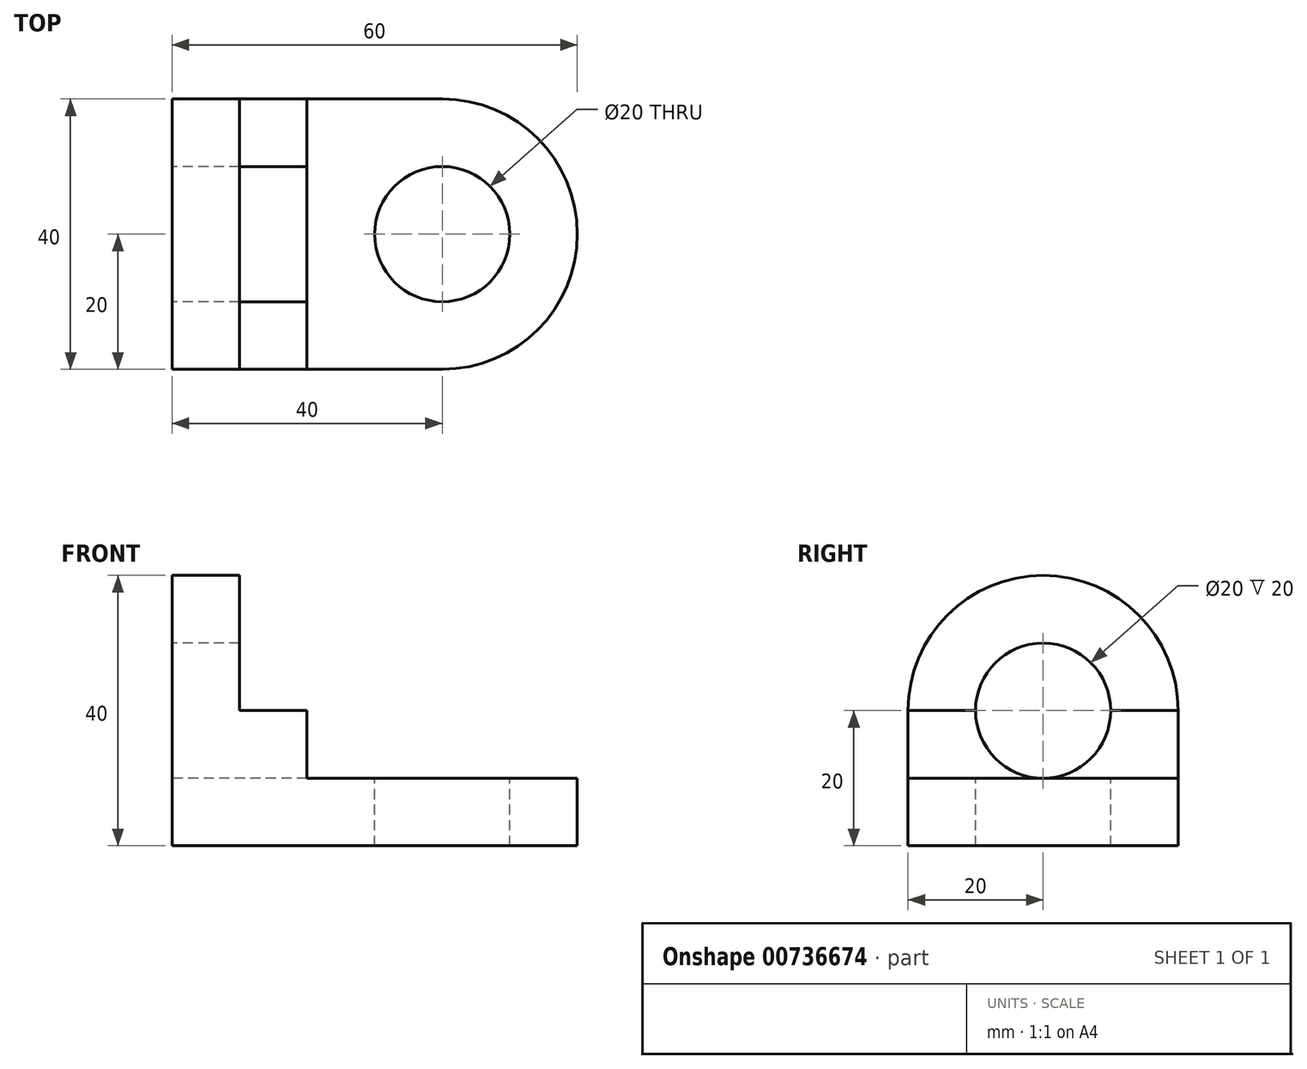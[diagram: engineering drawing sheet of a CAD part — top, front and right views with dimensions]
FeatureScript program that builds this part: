
annotation { "Feature Type Name" : "Feature", "Feature Type Description" : "" }
export const myFeature = defineFeature(function(context is Context, id is Id, definition is map)
    precondition{}
    {
        {
            var Q0;
            Q0=qCreatedBy(makeId("Right.planeOp"),FACE);
            var sketch = newSketch(context, id + "F0", { "sketchPlane" : qUnion([Q0])});
            skLineSegment(sketch, "E0", {"start": v(0, 0) * mm, "end": v(40, 0) * mm});
            skLineSegment(sketch, "E1", {"start": v(40, 0) * mm, "end": v(40, 40) * mm});
            skLineSegment(sketch, "E2", {"start": v(40, 40) * mm, "end": v(0, 40) * mm});
            skLineSegment(sketch, "E3", {"start": v(0, 40) * mm, "end": v(0, 0) * mm});
            skSolve(sketch);
        }
        {
            var Q0;
            Q0 = qSketchRegion(id + "F0", true);
            extrude(context, id + "F1", {"entities" : qUnion([Q0]), "depth" : 60 * mm, "offsetDistance" : 25 * mm});
        }
        {
            var Q0;
            Q0=makeQuery(id+"F1.opExtrude","SWEPT_FACE",FACE,{"disambiguationData":[OSD([sQuery(id+"F0.wireOp",EDGE,"E2")])]});
            var sketch = newSketch(context, id + "F2", { "sketchPlane" : qUnion([Q0])});
            skLineSegment(sketch, "E4", {"start": v(0, 40) * mm, "end": v(40, 40) * mm});
            skArc(sketch, "E5", {"start": v(40, 0) * mm, "mid": v(60, 20) * mm, "end": v(40, 40) * mm});
            skCircle(sketch, "E6", {"center": v(40, 20) * mm, "radius": 10 * mm});
            skSolve(sketch);
        }
        {
            var Q0;
            Q0=makeQuery(id+"F2.imprint","IMPRINT",FACE,{"disambiguationData":[TD([[makeQuery(id+"F2.imprint","IMPRINT",EDGE,{"derivedFrom":sQuery(id+"F2.wireOp",EDGE,"E6")}),1.0]])]});
            var Q1;
            {var subQ0=sQuery(id+"F2.wireOp",EDGE,"E5");var subQ1=sQuery(id+"F0.wireOp",EDGE,"E2");var subQ4=makeQuery(id+"F1.opExtrude","CAP_EDGE",EDGE,{"disambiguationData":[OSD([subQ1])],"isStart":false});var subQ5=makeQuery(id+"F2.imprint","INTERSECT",VERTEX,{"derivedFrom":[subQ4,subQ0]});Q1=makeQuery(id+"F2.imprint","IMPRINT",FACE,{"disambiguationData":[TD([[makeQuery(id+"F2.imprint","IMPRINT",EDGE,{"disambiguationData":[TD([[subQ5,1.0]])],"derivedFrom":subQ4}),-1.0]])]});}
            var Q2;
            {var subQ0=sQuery(id+"F2.wireOp",EDGE,"E5");var subQ1=sQuery(id+"F0.wireOp",EDGE,"E2");var subQ4=makeQuery(id+"F1.opExtrude","CAP_EDGE",EDGE,{"disambiguationData":[OSD([subQ1])],"isStart":false});var subQ5=makeQuery(id+"F2.imprint","INTERSECT",VERTEX,{"derivedFrom":[subQ4,subQ0]});Q2=makeQuery(id+"F2.imprint","IMPRINT",FACE,{"disambiguationData":[TD([[makeQuery(id+"F2.imprint","IMPRINT",EDGE,{"disambiguationData":[TD([[subQ5,1.0]])],"derivedFrom":subQ0}),-1.0]])]});}
            extrude(context, id + "F3", {"entities" : qUnion([Q0, Q1, Q2]), "operationType" : NewBodyOperationType.REMOVE, "oppositeDirection" : true, "depth" : 40 * mm, "offsetDistance" : 25 * mm});
        }
        {
            var Q0;
            Q0=makeQuery(id+"F1.opExtrude","CAP_FACE",FACE,{"disambiguationData":[OSD([sQuery(id+"F0.wireOp",EDGE,"E0"),sQuery(id+"F0.wireOp",EDGE,"E1"),sQuery(id+"F0.wireOp",EDGE,"E2"),sQuery(id+"F0.wireOp",EDGE,"E3")])],"isStart":true});
            var sketch = newSketch(context, id + "F4", { "sketchPlane" : qUnion([Q0])});
            skLineSegment(sketch, "E7", {"start": v(-40, 0) * mm, "end": v(-40, 20) * mm});
            skLineSegment(sketch, "E8", {"start": v(-40, 20) * mm, "end": v(-20, 20) * mm});
            skCircle(sketch, "E9", {"center": v(-20, 20) * mm, "radius": 10 * mm});
            skArc(sketch, "E10", {"start": v(0, 20) * mm, "mid": v(-20, 40) * mm, "end": v(-40, 20) * mm});
            skSolve(sketch);
        }
        {
            var Q0;
            Q0 = qSketchRegion(id + "F4", true);
            var Q1;
            {var subQ0=sQuery(id+"F4.wireOp",EDGE,"E10");var subQ1=makeQuery(id+"F1.opExtrude","CAP_EDGE",EDGE,{"disambiguationData":[OSD([sQuery(id+"F0.wireOp",EDGE,"E3")])],"isStart":true});var subQ2=makeQuery(id+"F4.imprint","INTERSECT",VERTEX,{"derivedFrom":[subQ1,subQ0]});Q1=makeQuery(id+"F4.imprint","IMPRINT",FACE,{"disambiguationData":[TD([[makeQuery(id+"F4.imprint","IMPRINT",EDGE,{"disambiguationData":[TD([[subQ2,-1.0]])],"derivedFrom":subQ0}),-1.0]])]});}
            var Q2;
            {var subQ1=makeQuery(id+"F1.opExtrude","CAP_EDGE",EDGE,{"disambiguationData":[OSD([sQuery(id+"F0.wireOp",EDGE,"E1")])],"isStart":true});var subQ3=makeQuery(id+"F1.opExtrude","CAP_EDGE",EDGE,{"disambiguationData":[OSD([sQuery(id+"F0.wireOp",EDGE,"E2")])],"isStart":true});var subQ5=makeQuery(id+"F4.imprint","INTERSECT",VERTEX,{"derivedFrom":[subQ1,subQ3]});Q2=makeQuery(id+"F4.imprint","IMPRINT",FACE,{"disambiguationData":[TD([[makeQuery(id+"F4.imprint","IMPRINT",EDGE,{"disambiguationData":[TD([[subQ5,-1.0]])],"derivedFrom":subQ3}),-1.0]])]});}
            extrude(context, id + "F5", {"entities" : qUnion([Q0, Q1, Q2]), "operationType" : NewBodyOperationType.REMOVE, "oppositeDirection" : true, "depth" : 60 * mm, "offsetDistance" : 25 * mm});
        }
        {
            var Q0;
            Q0=makeQuery(id+"F1.opExtrude","SWEPT_FACE",FACE,{"disambiguationData":[OSD([sQuery(id+"F0.wireOp",EDGE,"E3")])]});
            var sketch = newSketch(context, id + "F6", { "sketchPlane" : qUnion([Q0])});
            skLineSegment(sketch, "E11", {"start": v(0, 20) * mm, "end": v(20, 20) * mm});
            skLineSegment(sketch, "E12", {"start": v(20, 20) * mm, "end": v(20, 10) * mm});
            skLineSegment(sketch, "E13", {"start": v(20, 10) * mm, "end": v(60, 10) * mm});
            skLineSegment(sketch, "E14", {"start": v(60, 10) * mm, "end": v(60, 20) * mm});
            skLineSegment(sketch, "E15", {"start": v(60, 20) * mm, "end": v(20, 20) * mm});
            skLineSegment(sketch, "E16", {"start": v(10, 20) * mm, "end": v(10, 40) * mm});
            skLineSegment(sketch, "E17", {"start": v(10, 40) * mm, "end": v(60, 40) * mm});
            skLineSegment(sketch, "E18", {"start": v(60, 40) * mm, "end": v(60, 20) * mm});
            skSolve(sketch);
        }
        {
            var Q0;
            {var subQ0=sQuery(id+"F6.wireOp",EDGE,"E16");Q0=makeQuery(id+"F6.imprint","IMPRINT",FACE,{"disambiguationData":[TD([[makeQuery(id+"F6.imprint","IMPRINT",EDGE,{"derivedFrom":subQ0}),-1.0]])]});}
            var Q1;
            {var subQ0=sQuery(id+"F6.wireOp",EDGE,"E14");Q1=makeQuery(id+"F6.imprint","IMPRINT",FACE,{"disambiguationData":[TD([[makeQuery(id+"F6.imprint","IMPRINT",EDGE,{"derivedFrom":subQ0}),1.0]])]});}
            var Q2;
            {var subQ0=sQuery(id+"F6.wireOp",EDGE,"E12");Q2=makeQuery(id+"F6.imprint","IMPRINT",FACE,{"disambiguationData":[TD([[makeQuery(id+"F6.imprint","IMPRINT",EDGE,{"derivedFrom":subQ0}),1.0]])]});}
            extrude(context, id + "F7", {"entities" : qUnion([Q0, Q1, Q2]), "operationType" : NewBodyOperationType.REMOVE, "oppositeDirection" : true, "depth" : 40 * mm, "offsetDistance" : 25 * mm});
        }
    });
